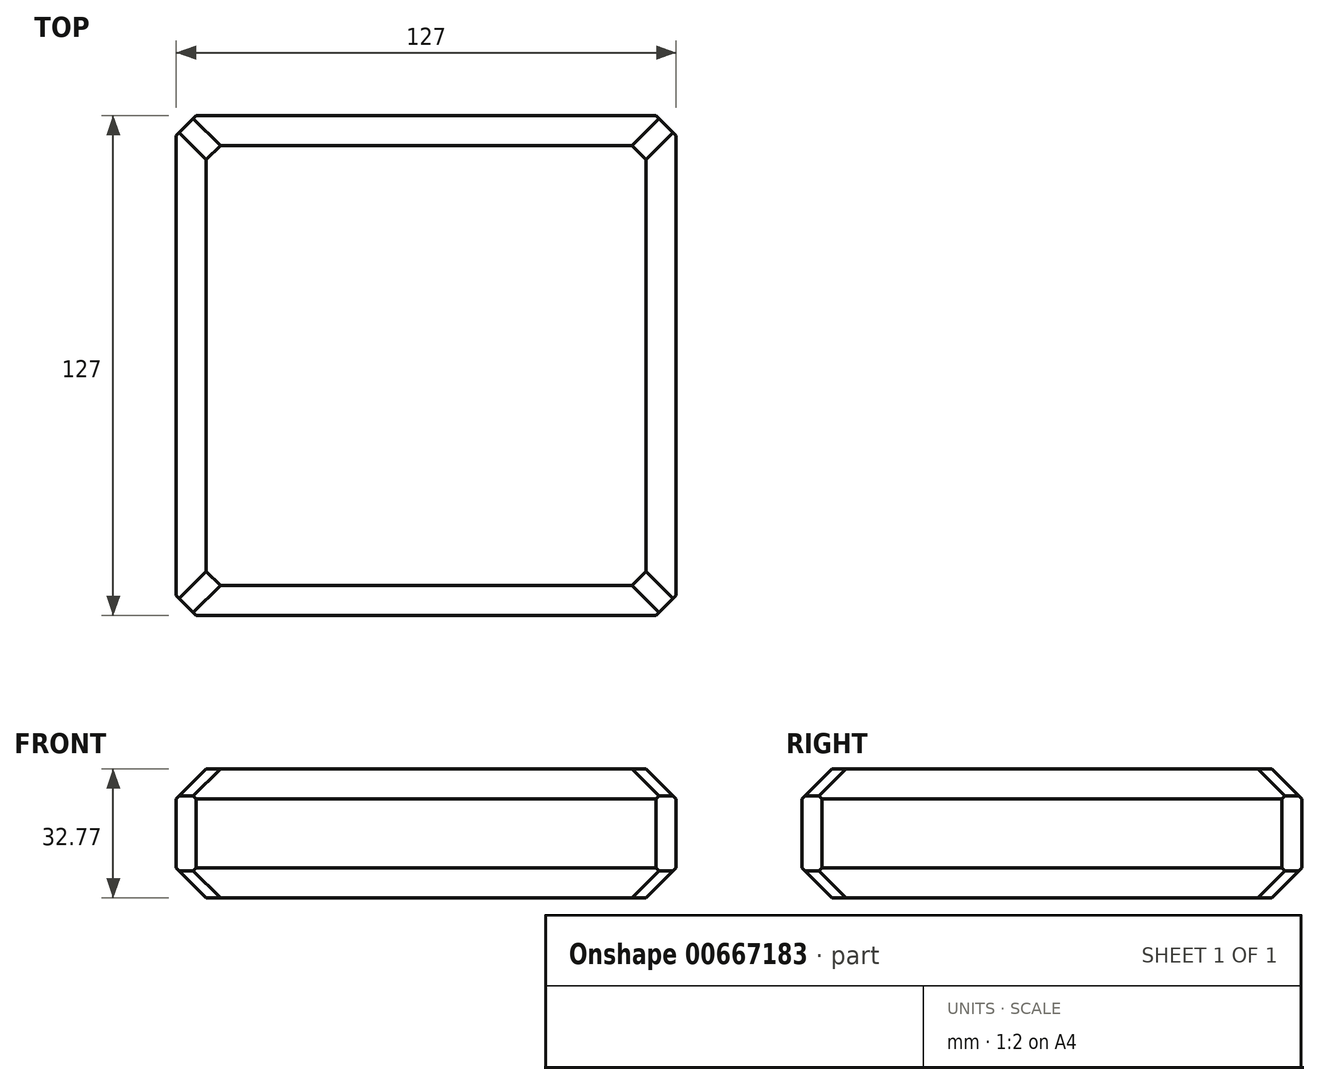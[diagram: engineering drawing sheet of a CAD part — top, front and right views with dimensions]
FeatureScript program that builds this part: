
annotation { "Feature Type Name" : "Feature", "Feature Type Description" : "" }
export const myFeature = defineFeature(function(context is Context, id is Id, definition is map)
    precondition{}
    {
        {
            var Q0;
            Q0=qCreatedBy(makeId("Top.planeOp"),FACE);
            var sketch = newSketch(context, id + "F0", { "sketchPlane" : qUnion([Q0])});
            skLineSegment(sketch, "E0.bottom", {"start": v(-52.05, 62.1) * mm, "end": v(74.95, 62.1) * mm});
            skLineSegment(sketch, "E0.top", {"start": v(-52.05, -64.9) * mm, "end": v(74.95, -64.9) * mm});
            skLineSegment(sketch, "E0.left", {"start": v(-52.05, 62.1) * mm, "end": v(-52.05, -64.9) * mm});
            skLineSegment(sketch, "E0.right", {"start": v(74.95, 62.1) * mm, "end": v(74.95, -64.9) * mm});
            skSolve(sketch);
        }
        {
            var Q0;
            Q0=makeQuery(id+"F0.imprint","IMPRINT",FACE,{"disambiguationData":[TD([[makeQuery(id+"F0.imprint","IMPRINT",EDGE,{"derivedFrom":sQuery(id+"F0.wireOp",EDGE,"E0.bottom")}),-1.0]])]});
            extrude(context, id + "F1", {"entities" : qUnion([Q0]), "depth" : 32.77 * mm, "offsetDistance" : 25.4 * mm});
        }
        {
            var Q0;
            Q0=makeQuery(id+"F1.opExtrude","CAP_EDGE",EDGE,{"disambiguationData":[OSD([sQuery(id+"F0.wireOp",EDGE,"E0.left")])],"isStart":false});
            var Q1;
            Q1=makeQuery(id+"F1.opExtrude","CAP_EDGE",EDGE,{"disambiguationData":[OSD([sQuery(id+"F0.wireOp",EDGE,"E0.bottom")])],"isStart":false});
            var Q2;
            Q2=makeQuery(id+"F1.opExtrude","CAP_EDGE",EDGE,{"disambiguationData":[OSD([sQuery(id+"F0.wireOp",EDGE,"E0.left")])],"isStart":true});
            var Q3;
            Q3=makeQuery(id+"F1.opExtrude","CAP_EDGE",EDGE,{"disambiguationData":[OSD([sQuery(id+"F0.wireOp",EDGE,"E0.right")])],"isStart":true});
            var Q4;
            Q4=makeQuery(id+"F1.opExtrude","CAP_EDGE",EDGE,{"disambiguationData":[OSD([sQuery(id+"F0.wireOp",EDGE,"E0.right")])],"isStart":false});
            var Q5;
            Q5=makeQuery(id+"F1.opExtrude","CAP_EDGE",EDGE,{"disambiguationData":[OSD([sQuery(id+"F0.wireOp",EDGE,"E0.top")])],"isStart":false});
            var Q6;
            Q6=makeQuery(id+"F1.opExtrude","CAP_EDGE",EDGE,{"disambiguationData":[OSD([sQuery(id+"F0.wireOp",EDGE,"E0.bottom")])],"isStart":true});
            var Q7;
            Q7=makeQuery(id+"F1.opExtrude","CAP_EDGE",EDGE,{"disambiguationData":[OSD([sQuery(id+"F0.wireOp",EDGE,"E0.top")])],"isStart":true});
            chamfer(context, id + "F2", {"entities" : qUnion([Q0, Q1, Q2, Q3, Q4, Q5, Q6, Q7]), "width" : 7.62 * mm, "tangentPropagation" : true});
        }
        {
            var Q0;
            Q0=makeQuery(id+"F2.opChamfer","BLEND_EDGE",EDGE,{"blendedFrom":[makeQuery(id+"F1.opExtrude","CAP_EDGE",EDGE,{"disambiguationData":[OSD([sQuery(id+"F0.wireOp",EDGE,"E0.bottom")])],"isStart":true}),makeQuery(id+"F1.opExtrude","CAP_EDGE",EDGE,{"disambiguationData":[OSD([sQuery(id+"F0.wireOp",EDGE,"E0.left")])],"isStart":true})],"blendedInto":[]});
            var Q1;
            Q1=makeQuery(id+"F1.opExtrude","SWEPT_EDGE",EDGE,{"disambiguationData":[OSD([sQuery(id+"F0.wireOp",EDGE,"E0.bottom"),sQuery(id+"F0.wireOp",EDGE,"E0.left")])]});
            var Q2;
            Q2=makeQuery(id+"F2.opChamfer","BLEND_EDGE",EDGE,{"blendedFrom":[makeQuery(id+"F1.opExtrude","CAP_EDGE",EDGE,{"disambiguationData":[OSD([sQuery(id+"F0.wireOp",EDGE,"E0.bottom")])],"isStart":false}),makeQuery(id+"F1.opExtrude","CAP_EDGE",EDGE,{"disambiguationData":[OSD([sQuery(id+"F0.wireOp",EDGE,"E0.left")])],"isStart":false})],"blendedInto":[]});
            var Q3;
            Q3=makeQuery(id+"F2.opChamfer","BLEND_EDGE",EDGE,{"blendedFrom":[makeQuery(id+"F1.opExtrude","CAP_EDGE",EDGE,{"disambiguationData":[OSD([sQuery(id+"F0.wireOp",EDGE,"E0.top")])],"isStart":true}),makeQuery(id+"F1.opExtrude","CAP_EDGE",EDGE,{"disambiguationData":[OSD([sQuery(id+"F0.wireOp",EDGE,"E0.left")])],"isStart":true})],"blendedInto":[]});
            var Q4;
            Q4=makeQuery(id+"F1.opExtrude","SWEPT_EDGE",EDGE,{"disambiguationData":[OSD([sQuery(id+"F0.wireOp",EDGE,"E0.top"),sQuery(id+"F0.wireOp",EDGE,"E0.left")])]});
            var Q5;
            Q5=makeQuery(id+"F2.opChamfer","BLEND_EDGE",EDGE,{"blendedFrom":[makeQuery(id+"F1.opExtrude","CAP_EDGE",EDGE,{"disambiguationData":[OSD([sQuery(id+"F0.wireOp",EDGE,"E0.top")])],"isStart":false}),makeQuery(id+"F1.opExtrude","CAP_EDGE",EDGE,{"disambiguationData":[OSD([sQuery(id+"F0.wireOp",EDGE,"E0.left")])],"isStart":false})],"blendedInto":[]});
            var Q6;
            Q6=makeQuery(id+"F2.opChamfer","BLEND_EDGE",EDGE,{"blendedFrom":[makeQuery(id+"F1.opExtrude","CAP_EDGE",EDGE,{"disambiguationData":[OSD([sQuery(id+"F0.wireOp",EDGE,"E0.top")])],"isStart":true}),makeQuery(id+"F1.opExtrude","CAP_EDGE",EDGE,{"disambiguationData":[OSD([sQuery(id+"F0.wireOp",EDGE,"E0.right")])],"isStart":true})],"blendedInto":[]});
            var Q7;
            Q7=makeQuery(id+"F1.opExtrude","SWEPT_EDGE",EDGE,{"disambiguationData":[OSD([sQuery(id+"F0.wireOp",EDGE,"E0.top"),sQuery(id+"F0.wireOp",EDGE,"E0.right")])]});
            var Q8;
            Q8=makeQuery(id+"F2.opChamfer","BLEND_EDGE",EDGE,{"blendedFrom":[makeQuery(id+"F1.opExtrude","CAP_EDGE",EDGE,{"disambiguationData":[OSD([sQuery(id+"F0.wireOp",EDGE,"E0.top")])],"isStart":false}),makeQuery(id+"F1.opExtrude","CAP_EDGE",EDGE,{"disambiguationData":[OSD([sQuery(id+"F0.wireOp",EDGE,"E0.right")])],"isStart":false})],"blendedInto":[]});
            var Q9;
            Q9=makeQuery(id+"F2.opChamfer","BLEND_EDGE",EDGE,{"blendedFrom":[makeQuery(id+"F1.opExtrude","CAP_EDGE",EDGE,{"disambiguationData":[OSD([sQuery(id+"F0.wireOp",EDGE,"E0.bottom")])],"isStart":true}),makeQuery(id+"F1.opExtrude","CAP_EDGE",EDGE,{"disambiguationData":[OSD([sQuery(id+"F0.wireOp",EDGE,"E0.right")])],"isStart":true})],"blendedInto":[]});
            var Q10;
            Q10=makeQuery(id+"F1.opExtrude","SWEPT_EDGE",EDGE,{"disambiguationData":[OSD([sQuery(id+"F0.wireOp",EDGE,"E0.bottom"),sQuery(id+"F0.wireOp",EDGE,"E0.right")])]});
            var Q11;
            Q11=makeQuery(id+"F2.opChamfer","BLEND_EDGE",EDGE,{"blendedFrom":[makeQuery(id+"F1.opExtrude","CAP_EDGE",EDGE,{"disambiguationData":[OSD([sQuery(id+"F0.wireOp",EDGE,"E0.bottom")])],"isStart":false}),makeQuery(id+"F1.opExtrude","CAP_EDGE",EDGE,{"disambiguationData":[OSD([sQuery(id+"F0.wireOp",EDGE,"E0.right")])],"isStart":false})],"blendedInto":[]});
            chamfer(context, id + "F3", {"entities" : qUnion([Q0, Q1, Q2, Q3, Q4, Q5, Q6, Q7, Q8, Q9, Q10, Q11]), "width" : 5.08 * mm, "tangentPropagation" : true});
        }
    });
